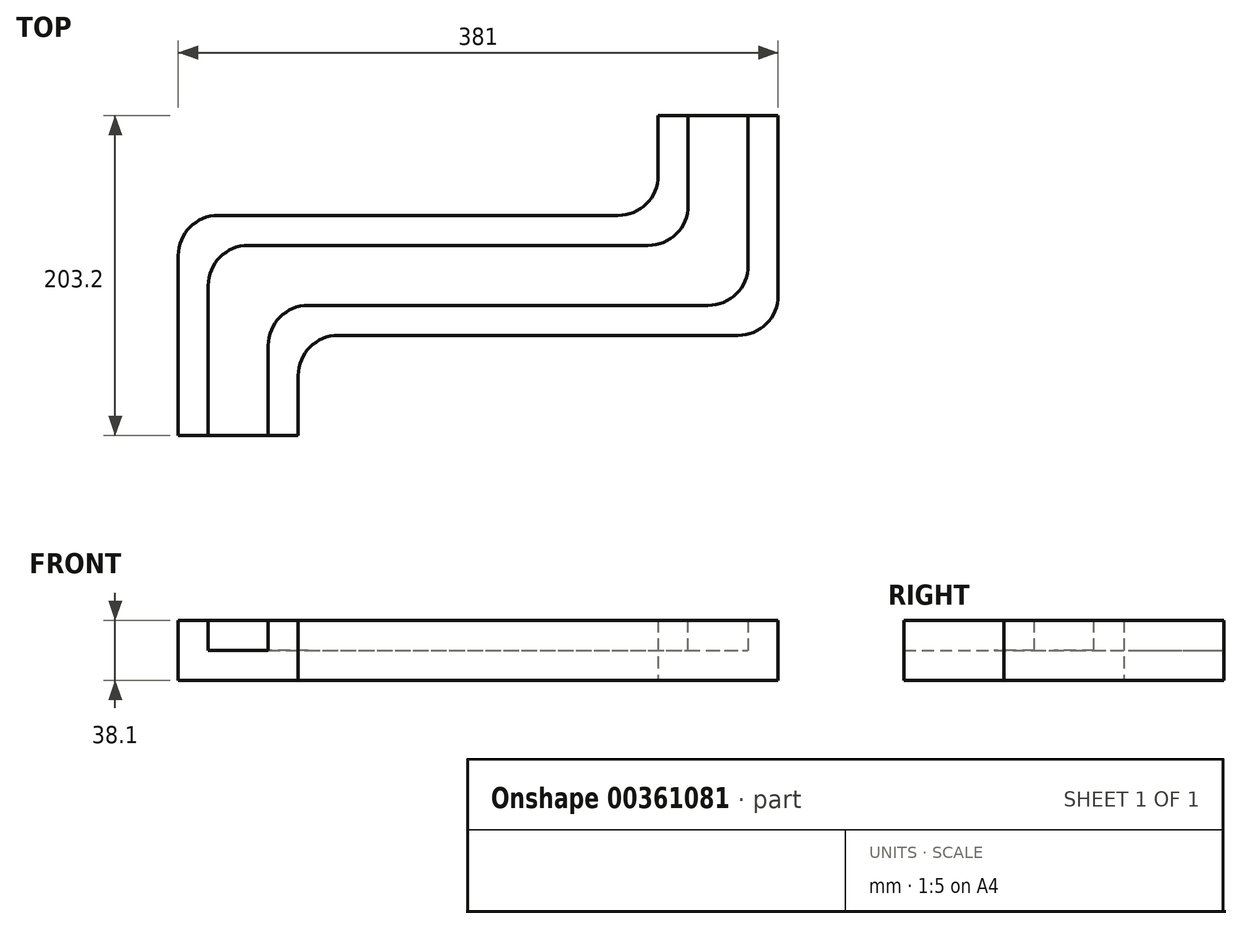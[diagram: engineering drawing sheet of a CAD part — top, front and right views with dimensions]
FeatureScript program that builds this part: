
annotation { "Feature Type Name" : "Feature", "Feature Type Description" : "" }
export const myFeature = defineFeature(function(context is Context, id is Id, definition is map)
    precondition{}
    {
        {
            var Q0;
            Q0=qCreatedBy(makeId("Front.planeOp"),FACE);
            var sketch = newSketch(context, id + "F0", { "sketchPlane" : qUnion([Q0])});
            skLineSegment(sketch, "E0.bottom", {"start": v(-38.1, 19.05) * mm, "end": v(-19.05, 19.05) * mm});
            skLineSegment(sketch, "E0.top", {"start": v(-38.1, -19.05) * mm, "end": v(38.1, -19.05) * mm});
            skLineSegment(sketch, "E0.left", {"start": v(-38.1, 19.05) * mm, "end": v(-38.1, -19.05) * mm});
            skLineSegment(sketch, "E0.right", {"start": v(38.1, 19.05) * mm, "end": v(38.1, -19.05) * mm});
            skLineSegment(sketch, "E1", {"start": v(-19.05, 19.05) * mm, "end": v(-19.05, 0) * mm});
            skLineSegment(sketch, "E2", {"start": v(-19.05, 0) * mm, "end": v(19.05, 0) * mm});
            skLineSegment(sketch, "E3", {"start": v(19.05, 0) * mm, "end": v(19.05, 19.05) * mm});
            skLineSegment(sketch, "E4.trimOffspring", {"start": v(19.05, 19.05) * mm, "end": v(38.1, 19.05) * mm});
            skSolve(sketch);
        }
        {
            var Q0;
            Q0=qCreatedBy(makeId("Top.planeOp"),FACE);
            var sketch = newSketch(context, id + "F1", { "sketchPlane" : qUnion([Q0])});
            skLineSegment(sketch, "E5", {"start": v(0, 0) * mm, "end": v(0, 101.6) * mm});
            skLineSegment(sketch, "E6", {"start": v(0, 101.6) * mm, "end": v(304.8, 101.6) * mm});
            skLineSegment(sketch, "E7", {"start": v(304.8, 101.6) * mm, "end": v(304.8, 203.2) * mm});
            skSolve(sketch);
        }
        {
            var Q0;
            Q0=makeQuery(id+"F0.imprint","IMPRINT",FACE,{"disambiguationData":[TD([[makeQuery(id+"F0.imprint","IMPRINT",EDGE,{"derivedFrom":sQuery(id+"F0.wireOp",EDGE,"E0.bottom")}),-1.0]])]});
            var Q1;
            Q1=sQuery(id+"F1.wireOp",EDGE,"E5");
            var Q2;
            Q2=sQuery(id+"F1.wireOp",EDGE,"E6");
            var Q3;
            Q3=sQuery(id+"F1.wireOp",EDGE,"E7");
            sweep(context, id + "F2", {"profiles" : qUnion([Q0]), "path" : qUnion([Q1, Q2, Q3])});
        }
        {
            var Q0;
            Q0=makeQuery(id+"F2.opSweep","MID_CAP_EDGE",EDGE,{"disambiguationData":[OSD([sQuery(id+"F0.wireOp",EDGE,"E0.right"),sQuery(id+"F1.wireOp",VERTEX,"E7.start")])],"capPos":2.0});
            var Q1;
            Q1=makeQuery(id+"F2.opSweep","MID_CAP_EDGE",EDGE,{"disambiguationData":[OSD([sQuery(id+"F0.wireOp",EDGE,"E0.right"),sQuery(id+"F1.wireOp",VERTEX,"E6.start")])],"capPos":1.0});
            var Q2;
            Q2=makeQuery(id+"F2.opSweep","MID_CAP_EDGE",EDGE,{"disambiguationData":[OSD([sQuery(id+"F0.wireOp",EDGE,"E0.left"),sQuery(id+"F1.wireOp",VERTEX,"E6.start")])],"capPos":1.0});
            var Q3;
            Q3=makeQuery(id+"F2.opSweep","MID_CAP_EDGE",EDGE,{"disambiguationData":[OSD([sQuery(id+"F0.wireOp",EDGE,"E0.left"),sQuery(id+"F1.wireOp",VERTEX,"E7.start")])],"capPos":2.0});
            var Q4;
            Q4=makeQuery(id+"F2.opSweep","MID_CAP_EDGE",EDGE,{"disambiguationData":[OSD([sQuery(id+"F0.wireOp",EDGE,"E1"),sQuery(id+"F1.wireOp",VERTEX,"E6.start")])],"capPos":1.0});
            var Q5;
            Q5=makeQuery(id+"F2.opSweep","MID_CAP_EDGE",EDGE,{"disambiguationData":[OSD([sQuery(id+"F0.wireOp",EDGE,"E1"),sQuery(id+"F1.wireOp",VERTEX,"E7.start")])],"capPos":2.0});
            var Q6;
            Q6=makeQuery(id+"F2.opSweep","MID_CAP_EDGE",EDGE,{"disambiguationData":[OSD([sQuery(id+"F0.wireOp",EDGE,"E3"),sQuery(id+"F1.wireOp",VERTEX,"E6.start")])],"capPos":1.0});
            var Q7;
            Q7=makeQuery(id+"F2.opSweep","MID_CAP_EDGE",EDGE,{"disambiguationData":[OSD([sQuery(id+"F0.wireOp",EDGE,"E3"),sQuery(id+"F1.wireOp",VERTEX,"E7.start")])],"capPos":2.0});
            fillet(context, id + "F3", {"entities" : qUnion([Q0, Q1, Q2, Q3, Q4, Q5, Q6, Q7]), "radius" : 25.4 * mm, "tangentPropagation" : true, "allowEdgeOverflow" : false});
        }
    });
